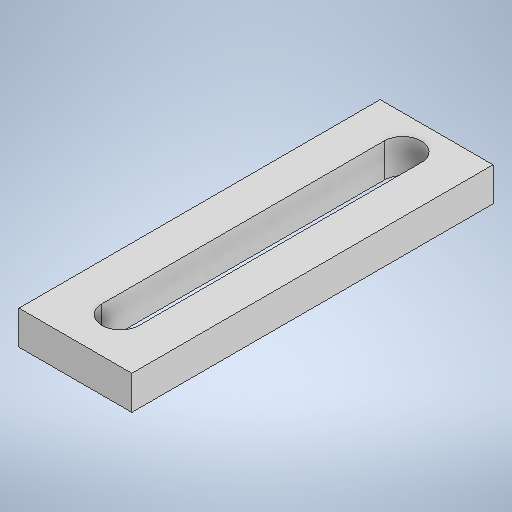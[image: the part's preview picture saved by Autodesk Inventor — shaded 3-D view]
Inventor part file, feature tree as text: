
AUTODESK INVENTOR PART (.ipt)
format: ipt  version: 2025.2 (Build 292293000, 293)  size: 218,112 bytes
history: native  units: mm
features: extrude x1, sketch x1
ambient origin geometry x8: Origin, YZ Plane, XZ Plane, XY Plane, X Axis, Y Axis, Z Axis, Center Point
bodies: Solid1 (feature_tree)
feature tree (2):
  extrude  "Extrusion1"  Depth=32.0mm
  sketch  "Sketch1"  dims[d0=10.0mm d1=32.0mm d2=4.0mm d3=3.0mm d4=3.3mm d5=3.0mm d6=0.0mm]
